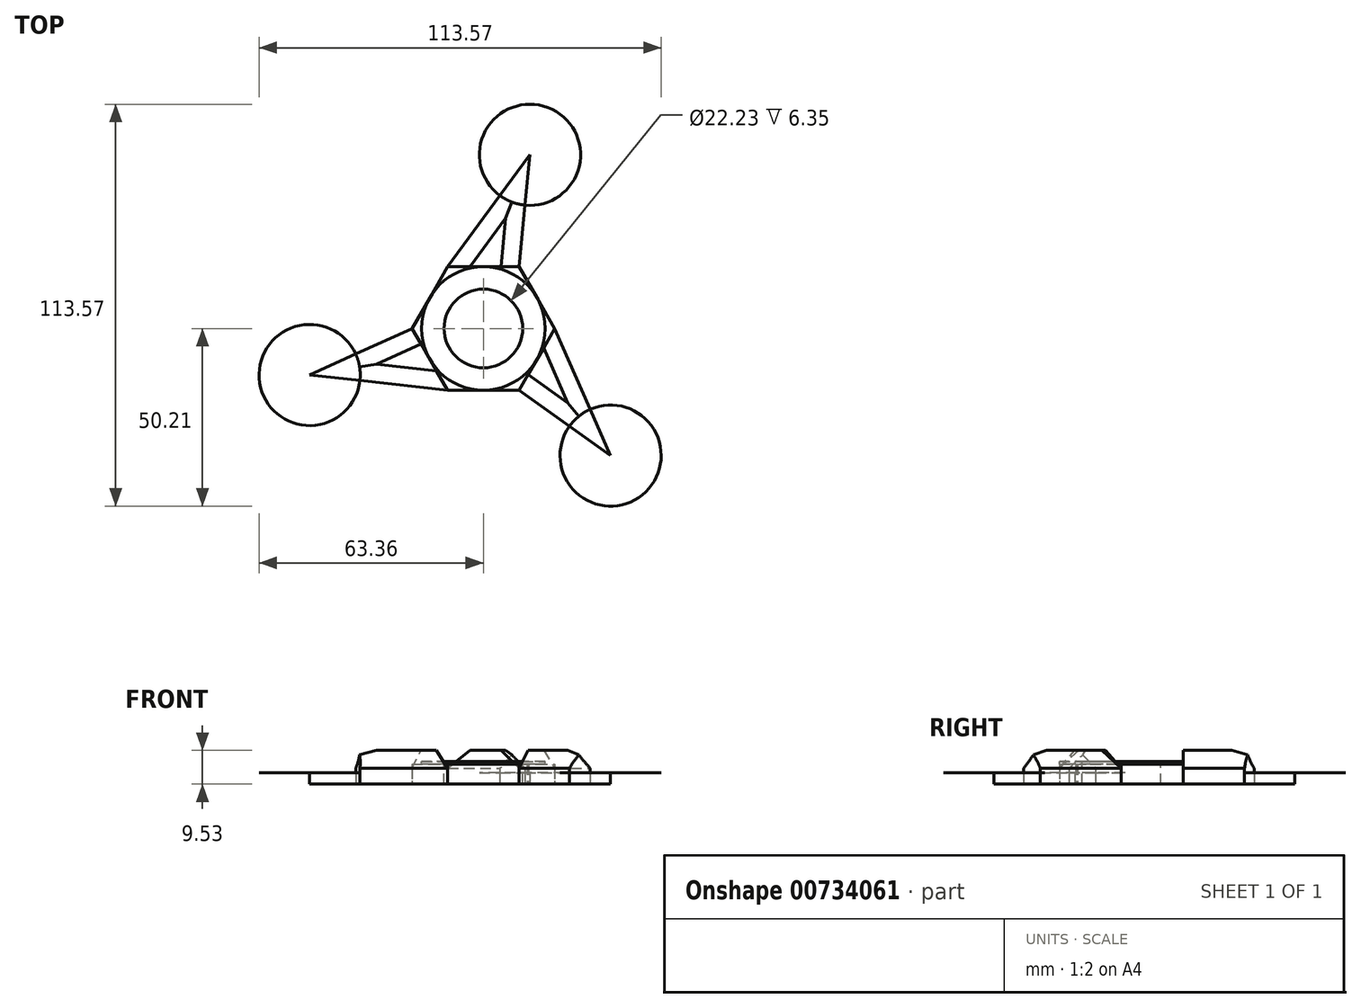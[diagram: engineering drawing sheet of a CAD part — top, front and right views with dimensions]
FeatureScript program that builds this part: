
annotation { "Feature Type Name" : "Feature", "Feature Type Description" : "" }
export const myFeature = defineFeature(function(context is Context, id is Id, definition is map)
    precondition{}
    {
        {
            var Q0;
            Q0=qCreatedBy(makeId("Top.planeOp"),FACE);
            var sketch = newSketch(context, id + "F0", { "sketchPlane" : qUnion([Q0])});
            skCircle(sketch, "E0", {"center": v(0, 0) * mm, "radius": 11.11 * mm});
            skCircle(sketch, "E1", {"center": v(0, 0) * mm, "radius": 17.46 * mm});
            skPoint(sketch, "E2.0.midPoint", {"position": v(15.12, 8.73) * mm});
            skCircle(sketch, "E3.cCircle", {"center": v(0, 0) * mm, "radius": 17.46 * mm, "construction": true});
            skLineSegment(sketch, "E3.0", {"start": v(10.08, 17.46) * mm, "end": v(20.16, 0) * mm});
            skLineSegment(sketch, "E3.1", {"start": v(20.16, 0) * mm, "end": v(10.08, -17.46) * mm});
            skLineSegment(sketch, "E3.2", {"start": v(10.08, -17.46) * mm, "end": v(-10.08, -17.46) * mm});
            skLineSegment(sketch, "E3.3", {"start": v(-10.08, -17.46) * mm, "end": v(-20.16, 0) * mm});
            skLineSegment(sketch, "E3.4", {"start": v(-20.16, 0) * mm, "end": v(-10.08, 17.46) * mm});
            skLineSegment(sketch, "E3.5", {"start": v(-10.08, 17.46) * mm, "end": v(10.08, 17.46) * mm});
            skLineSegment(sketch, "E4", {"start": v(-10.08, 17.46) * mm, "end": v(13.15, 49.07) * mm});
            skLineSegment(sketch, "E5", {"start": v(13.15, 49.07) * mm, "end": v(10.08, 17.46) * mm});
            skLineSegment(sketch, "E6", {"start": v(13.15, 49.07) * mm, "end": v(-13.15, -49.07) * mm});
            skLineSegment(sketch, "E7", {"start": v(-20.16, 0) * mm, "end": v(-49.07, -13.15) * mm});
            skLineSegment(sketch, "E8", {"start": v(-49.07, -13.15) * mm, "end": v(-10.08, -17.46) * mm});
            skLineSegment(sketch, "E9", {"start": v(-49.07, -13.15) * mm, "end": v(49.07, 13.15) * mm});
            skLineSegment(sketch, "E10", {"start": v(10.08, -17.46) * mm, "end": v(35.92, -35.92) * mm});
            skLineSegment(sketch, "E11", {"start": v(35.92, -35.92) * mm, "end": v(20.16, 0) * mm});
            skLineSegment(sketch, "E12", {"start": v(35.92, -35.92) * mm, "end": v(-35.92, 35.92) * mm});
            skCircle(sketch, "E13", {"center": v(-49.07, -13.15) * mm, "radius": 14.29 * mm});
            skCircle(sketch, "E14", {"center": v(35.92, -35.92) * mm, "radius": 14.29 * mm});
            skCircle(sketch, "E15", {"center": v(13.15, 49.07) * mm, "radius": 14.29 * mm});
            skSolve(sketch);
        }
        {
            var Q0;
            {var subQ0=sQuery(id+"F0.wireOp",EDGE,"E9");var subQ1=sQuery(id+"F0.wireOp",EDGE,"E0");var subQ2=makeQuery(id+"F0.imprint","INTERSECT",VERTEX,{"disambiguationData":[OD(1.0)],"derivedFrom":[subQ1,subQ0]});Q0=makeQuery(id+"F0.imprint","IMPRINT",FACE,{"disambiguationData":[TD([[makeQuery(id+"F0.imprint","IMPRINT",EDGE,{"disambiguationData":[TD([[subQ2,-1.0]])],"derivedFrom":subQ1}),-1.0]])]});}
            var Q1;
            {var subQ0=sQuery(id+"F0.wireOp",EDGE,"E6");var subQ1=sQuery(id+"F0.wireOp",EDGE,"E0");var subQ2=makeQuery(id+"F0.imprint","INTERSECT",VERTEX,{"disambiguationData":[OD(0.0)],"derivedFrom":[subQ1,subQ0]});Q1=makeQuery(id+"F0.imprint","IMPRINT",FACE,{"disambiguationData":[TD([[makeQuery(id+"F0.imprint","IMPRINT",EDGE,{"disambiguationData":[TD([[subQ2,-1.0]])],"derivedFrom":subQ1}),-1.0]])]});}
            var Q2;
            {var subQ0=sQuery(id+"F0.wireOp",EDGE,"E12");var subQ1=sQuery(id+"F0.wireOp",EDGE,"E0");var subQ2=makeQuery(id+"F0.imprint","INTERSECT",VERTEX,{"disambiguationData":[OD(0.0)],"derivedFrom":[subQ1,subQ0]});Q2=makeQuery(id+"F0.imprint","IMPRINT",FACE,{"disambiguationData":[TD([[makeQuery(id+"F0.imprint","IMPRINT",EDGE,{"disambiguationData":[TD([[subQ2,-1.0]])],"derivedFrom":subQ1}),-1.0]])]});}
            var Q3;
            {var subQ0=sQuery(id+"F0.wireOp",EDGE,"E6");var subQ1=sQuery(id+"F0.wireOp",EDGE,"E0");var subQ2=makeQuery(id+"F0.imprint","INTERSECT",VERTEX,{"disambiguationData":[OD(0.0)],"derivedFrom":[subQ1,subQ0]});Q3=makeQuery(id+"F0.imprint","IMPRINT",FACE,{"disambiguationData":[TD([[makeQuery(id+"F0.imprint","IMPRINT",EDGE,{"disambiguationData":[TD([[subQ2,1.0]])],"derivedFrom":subQ1}),-1.0]])]});}
            var Q4;
            {var subQ0=sQuery(id+"F0.wireOp",EDGE,"E9");var subQ1=sQuery(id+"F0.wireOp",EDGE,"E0");var subQ2=makeQuery(id+"F0.imprint","INTERSECT",VERTEX,{"disambiguationData":[OD(0.0)],"derivedFrom":[subQ1,subQ0]});Q4=makeQuery(id+"F0.imprint","IMPRINT",FACE,{"disambiguationData":[TD([[makeQuery(id+"F0.imprint","IMPRINT",EDGE,{"disambiguationData":[TD([[subQ2,1.0]])],"derivedFrom":subQ1}),-1.0]])]});}
            var Q5;
            {var subQ0=sQuery(id+"F0.wireOp",EDGE,"E6");var subQ1=sQuery(id+"F0.wireOp",EDGE,"E0");var subQ2=makeQuery(id+"F0.imprint","INTERSECT",VERTEX,{"disambiguationData":[OD(1.0)],"derivedFrom":[subQ1,subQ0]});Q5=makeQuery(id+"F0.imprint","IMPRINT",FACE,{"disambiguationData":[TD([[makeQuery(id+"F0.imprint","IMPRINT",EDGE,{"disambiguationData":[TD([[subQ2,-1.0]])],"derivedFrom":subQ1}),-1.0]])]});}
            extrude(context, id + "F1", {"entities" : qUnion([Q0, Q1, Q2, Q3, Q4, Q5]), "oppositeDirection" : true, "depth" : 3.17 * mm, "offsetDistance" : 25.4 * mm, "hasSecondDirection" : true, "secondDirectionOppositeDirection" : false, "secondDirectionDepth" : 3.17 * mm});
        }
        {
            var Q0;
            {var subQ0=sQuery(id+"F0.wireOp",EDGE,"E3.0");var subQ1=sQuery(id+"F0.wireOp",EDGE,"E1");var subQ2=makeQuery(id+"F0.imprint","INTERSECT",VERTEX,{"derivedFrom":[subQ1,subQ0]});Q0=makeQuery(id+"F0.imprint","IMPRINT",FACE,{"disambiguationData":[TD([[makeQuery(id+"F0.imprint","IMPRINT",EDGE,{"disambiguationData":[TD([[subQ2,-1.0]])],"derivedFrom":subQ1}),-1.0]])]});}
            var Q1;
            {var subQ0=sQuery(id+"F0.wireOp",EDGE,"E9");var subQ1=sQuery(id+"F0.wireOp",EDGE,"E1");var subQ2=makeQuery(id+"F0.imprint","INTERSECT",VERTEX,{"disambiguationData":[OD(0.0)],"derivedFrom":[subQ1,subQ0]});Q1=makeQuery(id+"F0.imprint","IMPRINT",FACE,{"disambiguationData":[TD([[makeQuery(id+"F0.imprint","IMPRINT",EDGE,{"disambiguationData":[TD([[subQ2,1.0]])],"derivedFrom":subQ1}),-1.0]])]});}
            var Q2;
            {var subQ0=sQuery(id+"F0.wireOp",EDGE,"E3.2");var subQ1=sQuery(id+"F0.wireOp",EDGE,"E1");var subQ2=makeQuery(id+"F0.imprint","INTERSECT",VERTEX,{"derivedFrom":[subQ1,subQ0]});Q2=makeQuery(id+"F0.imprint","IMPRINT",FACE,{"disambiguationData":[TD([[makeQuery(id+"F0.imprint","IMPRINT",EDGE,{"disambiguationData":[TD([[subQ2,-1.0]])],"derivedFrom":subQ1}),-1.0]])]});}
            var Q3;
            {var subQ0=sQuery(id+"F0.wireOp",EDGE,"E3.3");var subQ1=sQuery(id+"F0.wireOp",EDGE,"E1");var subQ2=makeQuery(id+"F0.imprint","INTERSECT",VERTEX,{"derivedFrom":[subQ1,subQ0]});Q3=makeQuery(id+"F0.imprint","IMPRINT",FACE,{"disambiguationData":[TD([[makeQuery(id+"F0.imprint","IMPRINT",EDGE,{"disambiguationData":[TD([[subQ2,-1.0]])],"derivedFrom":subQ1}),-1.0]])]});}
            var Q4;
            {var subQ0=sQuery(id+"F0.wireOp",EDGE,"E3.4");var subQ1=sQuery(id+"F0.wireOp",EDGE,"E1");var subQ2=makeQuery(id+"F0.imprint","INTERSECT",VERTEX,{"derivedFrom":[subQ1,subQ0]});Q4=makeQuery(id+"F0.imprint","IMPRINT",FACE,{"disambiguationData":[TD([[makeQuery(id+"F0.imprint","IMPRINT",EDGE,{"disambiguationData":[TD([[subQ2,-1.0]])],"derivedFrom":subQ1}),-1.0]])]});}
            var Q5;
            {var subQ0=sQuery(id+"F0.wireOp",EDGE,"E3.5");var subQ1=sQuery(id+"F0.wireOp",EDGE,"E1");var subQ2=makeQuery(id+"F0.imprint","INTERSECT",VERTEX,{"derivedFrom":[subQ1,subQ0]});Q5=makeQuery(id+"F0.imprint","IMPRINT",FACE,{"disambiguationData":[TD([[makeQuery(id+"F0.imprint","IMPRINT",EDGE,{"disambiguationData":[TD([[subQ2,-1.0]])],"derivedFrom":subQ1}),-1.0]])]});}
            var Q6;
            {var subQ0=sQuery(id+"F0.wireOp",EDGE,"E3.4");var subQ1=sQuery(id+"F0.wireOp",EDGE,"E1");var subQ2=makeQuery(id+"F0.imprint","INTERSECT",VERTEX,{"derivedFrom":[subQ1,subQ0]});Q6=makeQuery(id+"F0.imprint","IMPRINT",FACE,{"disambiguationData":[TD([[makeQuery(id+"F0.imprint","IMPRINT",EDGE,{"disambiguationData":[TD([[subQ2,1.0]])],"derivedFrom":subQ1}),-1.0]])]});}
            var Q7;
            {var subQ0=sQuery(id+"F0.wireOp",EDGE,"E9");var subQ1=sQuery(id+"F0.wireOp",EDGE,"E1");var subQ2=makeQuery(id+"F0.imprint","INTERSECT",VERTEX,{"disambiguationData":[OD(1.0)],"derivedFrom":[subQ1,subQ0]});Q7=makeQuery(id+"F0.imprint","IMPRINT",FACE,{"disambiguationData":[TD([[makeQuery(id+"F0.imprint","IMPRINT",EDGE,{"disambiguationData":[TD([[subQ2,-1.0]])],"derivedFrom":subQ1}),-1.0]])]});}
            var Q8;
            {var subQ0=sQuery(id+"F0.wireOp",EDGE,"E3.2");var subQ1=sQuery(id+"F0.wireOp",EDGE,"E1");var subQ2=makeQuery(id+"F0.imprint","INTERSECT",VERTEX,{"derivedFrom":[subQ1,subQ0]});Q8=makeQuery(id+"F0.imprint","IMPRINT",FACE,{"disambiguationData":[TD([[makeQuery(id+"F0.imprint","IMPRINT",EDGE,{"disambiguationData":[TD([[subQ2,1.0]])],"derivedFrom":subQ1}),-1.0]])]});}
            var Q9;
            {var subQ0=sQuery(id+"F0.wireOp",EDGE,"E12");var subQ1=sQuery(id+"F0.wireOp",EDGE,"E1");var subQ2=makeQuery(id+"F0.imprint","INTERSECT",VERTEX,{"disambiguationData":[OD(1.0)],"derivedFrom":[subQ1,subQ0]});Q9=makeQuery(id+"F0.imprint","IMPRINT",FACE,{"disambiguationData":[TD([[makeQuery(id+"F0.imprint","IMPRINT",EDGE,{"disambiguationData":[TD([[subQ2,-1.0]])],"derivedFrom":subQ1}),-1.0]])]});}
            var Q10;
            {var subQ0=sQuery(id+"F0.wireOp",EDGE,"E3.0");var subQ1=sQuery(id+"F0.wireOp",EDGE,"E1");var subQ2=makeQuery(id+"F0.imprint","INTERSECT",VERTEX,{"derivedFrom":[subQ1,subQ0]});Q10=makeQuery(id+"F0.imprint","IMPRINT",FACE,{"disambiguationData":[TD([[makeQuery(id+"F0.imprint","IMPRINT",EDGE,{"disambiguationData":[TD([[subQ2,1.0]])],"derivedFrom":subQ1}),-1.0]])]});}
            var Q11;
            {var subQ0=sQuery(id+"F0.wireOp",EDGE,"E6");var subQ1=sQuery(id+"F0.wireOp",EDGE,"E1");var subQ2=makeQuery(id+"F0.imprint","INTERSECT",VERTEX,{"disambiguationData":[OD(0.0)],"derivedFrom":[subQ1,subQ0]});Q11=makeQuery(id+"F0.imprint","IMPRINT",FACE,{"disambiguationData":[TD([[makeQuery(id+"F0.imprint","IMPRINT",EDGE,{"disambiguationData":[TD([[subQ2,-1.0]])],"derivedFrom":subQ1}),-1.0]])]});}
            extrude(context, id + "F2", {"entities" : qUnion([Q0, Q1, Q2, Q3, Q4, Q5, Q6, Q7, Q8, Q9, Q10, Q11]), "operationType" : NewBodyOperationType.ADD, "depth" : 2.38 * mm, "offsetDistance" : 25.4 * mm, "hasSecondDirection" : true, "secondDirectionOppositeDirection" : true, "secondDirectionDepth" : 3.17 * mm});
        }
        {
            var Q0;
            {var subQ0=sQuery(id+"F0.wireOp",EDGE,"E10");var subQ5=sQuery(id+"F0.wireOp",EDGE,"E14");var subQ6=makeQuery(id+"F0.imprint","INTERSECT",VERTEX,{"derivedFrom":[subQ0,subQ5]});Q0=makeQuery(id+"F0.imprint","IMPRINT",FACE,{"disambiguationData":[TD([[makeQuery(id+"F0.imprint","IMPRINT",EDGE,{"disambiguationData":[TD([[subQ6,1.0]])],"derivedFrom":subQ5}),-1.0]])]});}
            var Q1;
            {var subQ0=sQuery(id+"F0.wireOp",EDGE,"E11");var subQ5=sQuery(id+"F0.wireOp",EDGE,"E14");var subQ7=makeQuery(id+"F0.imprint","INTERSECT",VERTEX,{"derivedFrom":[subQ0,subQ5]});Q1=makeQuery(id+"F0.imprint","IMPRINT",FACE,{"disambiguationData":[TD([[makeQuery(id+"F0.imprint","IMPRINT",EDGE,{"disambiguationData":[TD([[subQ7,-1.0]])],"derivedFrom":subQ5}),-1.0]])]});}
            var Q2;
            {var subQ0=sQuery(id+"F0.wireOp",EDGE,"E5");var subQ5=sQuery(id+"F0.wireOp",EDGE,"E15");var subQ6=makeQuery(id+"F0.imprint","INTERSECT",VERTEX,{"derivedFrom":[subQ0,subQ5]});Q2=makeQuery(id+"F0.imprint","IMPRINT",FACE,{"disambiguationData":[TD([[makeQuery(id+"F0.imprint","IMPRINT",EDGE,{"disambiguationData":[TD([[subQ6,1.0]])],"derivedFrom":subQ5}),-1.0]])]});}
            var Q3;
            {var subQ0=sQuery(id+"F0.wireOp",EDGE,"E4");var subQ5=sQuery(id+"F0.wireOp",EDGE,"E15");var subQ6=makeQuery(id+"F0.imprint","INTERSECT",VERTEX,{"derivedFrom":[subQ0,subQ5]});Q3=makeQuery(id+"F0.imprint","IMPRINT",FACE,{"disambiguationData":[TD([[makeQuery(id+"F0.imprint","IMPRINT",EDGE,{"disambiguationData":[TD([[subQ6,-1.0]])],"derivedFrom":subQ5}),-1.0]])]});}
            var Q4;
            {var subQ0=sQuery(id+"F0.wireOp",EDGE,"E8");var subQ5=sQuery(id+"F0.wireOp",EDGE,"E13");var subQ6=makeQuery(id+"F0.imprint","INTERSECT",VERTEX,{"derivedFrom":[subQ0,subQ5]});Q4=makeQuery(id+"F0.imprint","IMPRINT",FACE,{"disambiguationData":[TD([[makeQuery(id+"F0.imprint","IMPRINT",EDGE,{"disambiguationData":[TD([[subQ6,-1.0]])],"derivedFrom":subQ5}),-1.0]])]});}
            var Q5;
            {var subQ0=sQuery(id+"F0.wireOp",EDGE,"E7");var subQ5=sQuery(id+"F0.wireOp",EDGE,"E13");var subQ6=makeQuery(id+"F0.imprint","INTERSECT",VERTEX,{"derivedFrom":[subQ0,subQ5]});Q5=makeQuery(id+"F0.imprint","IMPRINT",FACE,{"disambiguationData":[TD([[makeQuery(id+"F0.imprint","IMPRINT",EDGE,{"disambiguationData":[TD([[subQ6,1.0]])],"derivedFrom":subQ5}),-1.0]])]});}
            extrude(context, id + "F3", {"entities" : qUnion([Q0, Q1, Q2, Q3, Q4, Q5]), "surfaceOperationType" : NewSurfaceOperationType.ADD, "depth" : 6.35 * mm, "offsetDistance" : 25.4 * mm, "hasSecondDirection" : true, "secondDirectionOppositeDirection" : true, "secondDirectionDepth" : 3.17 * mm});
        }
        {
            var Q0;
            {var subQ1=sQuery(id+"F0.wireOp",EDGE,"E4");var subQ3=sQuery(id+"F0.wireOp",EDGE,"E15");var subQ4=makeQuery(id+"F0.imprint","INTERSECT",VERTEX,{"derivedFrom":[subQ1,subQ3]});Q0=makeQuery(id+"F0.imprint","IMPRINT",FACE,{"disambiguationData":[TD([[makeQuery(id+"F0.imprint","IMPRINT",EDGE,{"disambiguationData":[TD([[subQ4,1.0]])],"derivedFrom":subQ3}),1.0]])]});}
            var Q1;
            {var subQ1=sQuery(id+"F0.wireOp",EDGE,"E7");var subQ3=sQuery(id+"F0.wireOp",EDGE,"E13");var subQ4=makeQuery(id+"F0.imprint","INTERSECT",VERTEX,{"derivedFrom":[subQ1,subQ3]});Q1=makeQuery(id+"F0.imprint","IMPRINT",FACE,{"disambiguationData":[TD([[makeQuery(id+"F0.imprint","IMPRINT",EDGE,{"disambiguationData":[TD([[subQ4,-1.0]])],"derivedFrom":subQ3}),1.0]])]});}
            var Q2;
            {var subQ1=sQuery(id+"F0.wireOp",EDGE,"E10");var subQ3=sQuery(id+"F0.wireOp",EDGE,"E14");var subQ4=makeQuery(id+"F0.imprint","INTERSECT",VERTEX,{"derivedFrom":[subQ1,subQ3]});Q2=makeQuery(id+"F0.imprint","IMPRINT",FACE,{"disambiguationData":[TD([[makeQuery(id+"F0.imprint","IMPRINT",EDGE,{"disambiguationData":[TD([[subQ4,-1.0]])],"derivedFrom":subQ3}),1.0]])]});}
            extrude(context, id + "F4", {"entities" : qUnion([Q0, Q1, Q2]), "depth" : 5 / 812.8 * mm, "offsetDistance" : 25.4 * mm, "hasSecondDirection" : true, "secondDirectionOppositeDirection" : true, "secondDirectionDepth" : 5 / 812.8 * mm});
        }
        {
            var Q0;
            {var subQ1=sQuery(id+"F0.wireOp",EDGE,"E10");var subQ3=sQuery(id+"F0.wireOp",EDGE,"E14");var subQ4=makeQuery(id+"F0.imprint","INTERSECT",VERTEX,{"derivedFrom":[subQ1,subQ3]});Q0=makeQuery(id+"F0.imprint","IMPRINT",FACE,{"disambiguationData":[TD([[makeQuery(id+"F0.imprint","IMPRINT",EDGE,{"disambiguationData":[TD([[subQ4,1.0]])],"derivedFrom":subQ3}),1.0]])]});}
            var Q1;
            {var subQ1=sQuery(id+"F0.wireOp",EDGE,"E11");var subQ3=sQuery(id+"F0.wireOp",EDGE,"E14");var subQ4=makeQuery(id+"F0.imprint","INTERSECT",VERTEX,{"derivedFrom":[subQ1,subQ3]});Q1=makeQuery(id+"F0.imprint","IMPRINT",FACE,{"disambiguationData":[TD([[makeQuery(id+"F0.imprint","IMPRINT",EDGE,{"disambiguationData":[TD([[subQ4,-1.0]])],"derivedFrom":subQ3}),1.0]])]});}
            var Q2;
            {var subQ1=sQuery(id+"F0.wireOp",EDGE,"E5");var subQ3=sQuery(id+"F0.wireOp",EDGE,"E15");var subQ4=makeQuery(id+"F0.imprint","INTERSECT",VERTEX,{"derivedFrom":[subQ1,subQ3]});Q2=makeQuery(id+"F0.imprint","IMPRINT",FACE,{"disambiguationData":[TD([[makeQuery(id+"F0.imprint","IMPRINT",EDGE,{"disambiguationData":[TD([[subQ4,1.0]])],"derivedFrom":subQ3}),1.0]])]});}
            var Q3;
            {var subQ1=sQuery(id+"F0.wireOp",EDGE,"E4");var subQ3=sQuery(id+"F0.wireOp",EDGE,"E15");var subQ4=makeQuery(id+"F0.imprint","INTERSECT",VERTEX,{"derivedFrom":[subQ1,subQ3]});Q3=makeQuery(id+"F0.imprint","IMPRINT",FACE,{"disambiguationData":[TD([[makeQuery(id+"F0.imprint","IMPRINT",EDGE,{"disambiguationData":[TD([[subQ4,-1.0]])],"derivedFrom":subQ3}),1.0]])]});}
            var Q4;
            {var subQ1=sQuery(id+"F0.wireOp",EDGE,"E7");var subQ3=sQuery(id+"F0.wireOp",EDGE,"E13");var subQ4=makeQuery(id+"F0.imprint","INTERSECT",VERTEX,{"derivedFrom":[subQ1,subQ3]});Q4=makeQuery(id+"F0.imprint","IMPRINT",FACE,{"disambiguationData":[TD([[makeQuery(id+"F0.imprint","IMPRINT",EDGE,{"disambiguationData":[TD([[subQ4,1.0]])],"derivedFrom":subQ3}),1.0]])]});}
            var Q5;
            {var subQ1=sQuery(id+"F0.wireOp",EDGE,"E8");var subQ3=sQuery(id+"F0.wireOp",EDGE,"E13");var subQ4=makeQuery(id+"F0.imprint","INTERSECT",VERTEX,{"derivedFrom":[subQ1,subQ3]});Q5=makeQuery(id+"F0.imprint","IMPRINT",FACE,{"disambiguationData":[TD([[makeQuery(id+"F0.imprint","IMPRINT",EDGE,{"disambiguationData":[TD([[subQ4,-1.0]])],"derivedFrom":subQ3}),1.0]])]});}
            extrude(context, id + "F5", {"entities" : qUnion([Q0, Q1, Q2, Q3, Q4, Q5]), "depth" : 3 / 812.8 * mm, "offsetDistance" : 25.4 * mm, "hasSecondDirection" : true, "secondDirectionOppositeDirection" : true, "secondDirectionDepth" : 3.17 * mm});
        }
        {
            var Q0;
            Q0=makeQuery(id+"F3.opExtrude","CAP_EDGE",EDGE,{"disambiguationData":[OSD([sQuery(id+"F0.wireOp",EDGE,"E11")])],"isStart":false});
            var Q1;
            Q1=makeQuery(id+"F3.opExtrude","CAP_EDGE",EDGE,{"disambiguationData":[OSD([sQuery(id+"F0.wireOp",EDGE,"E10")])],"isStart":false});
            var Q2;
            Q2=makeQuery(id+"F3.opExtrude","CAP_EDGE",EDGE,{"disambiguationData":[OSD([sQuery(id+"F0.wireOp",EDGE,"E5")])],"isStart":false});
            var Q3;
            Q3=makeQuery(id+"F3.opExtrude","CAP_EDGE",EDGE,{"disambiguationData":[OSD([sQuery(id+"F0.wireOp",EDGE,"E4")])],"isStart":false});
            var Q4;
            Q4=makeQuery(id+"F3.opExtrude","CAP_EDGE",EDGE,{"disambiguationData":[OSD([sQuery(id+"F0.wireOp",EDGE,"E7")])],"isStart":false});
            var Q5;
            Q5=makeQuery(id+"F3.opExtrude","CAP_EDGE",EDGE,{"disambiguationData":[OSD([sQuery(id+"F0.wireOp",EDGE,"E8")])],"isStart":false});
            var Q6;
            Q6=makeQuery(id+"F4.opExtrude","CAP_FACE",FACE,{"disambiguationData":[OSD([sQuery(id+"F0.wireOp",EDGE,"E7"),sQuery(id+"F0.wireOp",EDGE,"E8"),sQuery(id+"F0.wireOp",EDGE,"E13")])],"isStart":false});
            var Q7;
            Q7=makeQuery(id+"F4.opExtrude","CAP_FACE",FACE,{"disambiguationData":[OSD([sQuery(id+"F0.wireOp",EDGE,"E10"),sQuery(id+"F0.wireOp",EDGE,"E11"),sQuery(id+"F0.wireOp",EDGE,"E14")])],"isStart":false});
            var Q8;
            Q8=makeQuery(id+"F4.opExtrude","CAP_FACE",FACE,{"disambiguationData":[OSD([sQuery(id+"F0.wireOp",EDGE,"E4"),sQuery(id+"F0.wireOp",EDGE,"E5"),sQuery(id+"F0.wireOp",EDGE,"E15")])],"isStart":false});
            chamfer(context, id + "F6", {"entities" : qUnion([Q0, Q1, Q2, Q3, Q4, Q5, Q6, Q7, Q8]), "width" : 5.08 * mm, "tangentPropagation" : true});
        }
    });
